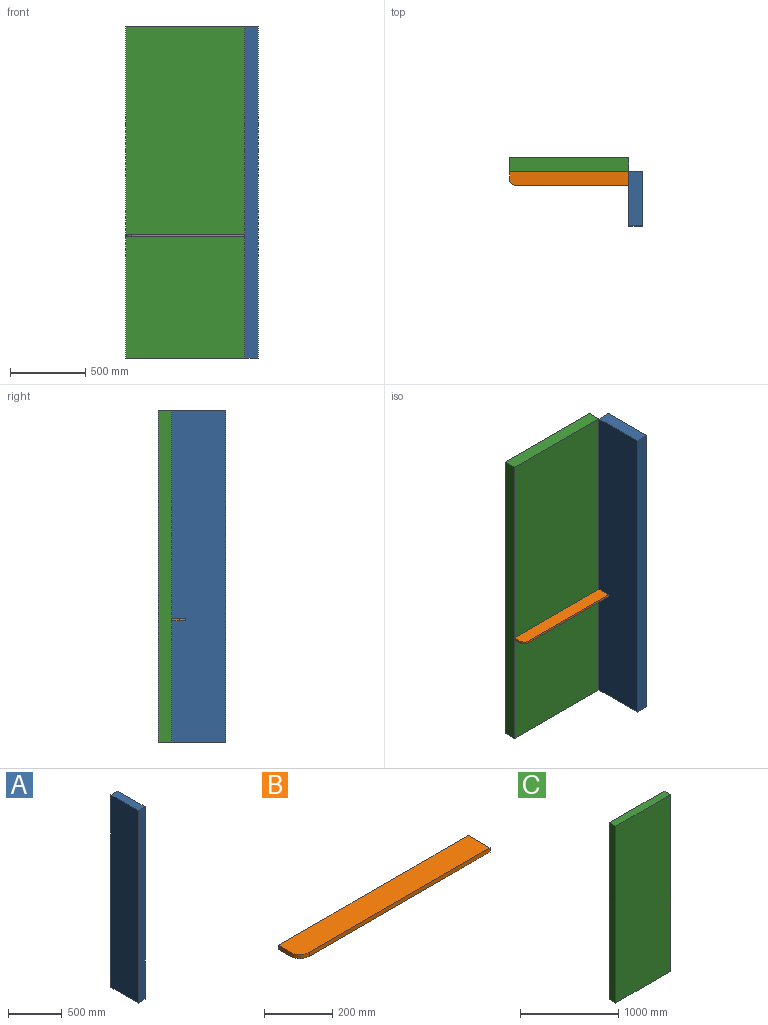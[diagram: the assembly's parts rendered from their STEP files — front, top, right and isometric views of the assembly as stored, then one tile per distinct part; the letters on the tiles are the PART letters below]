
ASSEMBLY  parts=3 mates=2
PART A: 6 faces, bbox 90x360x2200 mm
  f0: plane 360x90mm, normal (0,0,-1), area 32400mm2, adj f1,f3,f4,f5
  f1: plane 2200x90mm, normal (0,1,0), area 198000mm2, adj f0,f2,f4,f5
  f2: plane 360x90mm, normal (0,0,1), area 32400mm2, adj f1,f3,f4,f5
  f3: plane 2200x90mm, normal (0,-1,0), area 198000mm2, adj f0,f2,f4,f5
  f4: plane 2200x360mm, normal (1,0,0), area 792000mm2, adj f0,f1,f2,f3
  f5: plane 2200x360mm, normal (-1,0,0), area 792000mm2, adj f0,f1,f2,f3
PART B: 7 faces, bbox 790x90x15 mm
  f0: plane 50x15mm, normal (-1,0,0), area 750mm2, adj f1,f4,f5,f6
  f1: cylinder r=40mm len=40mm, axis (0,0,-1), area 942.5mm2, adj f0,f2,f5,f6
  f2: plane 750x15mm, normal (0,-1,0), area 11250mm2, adj f1,f3,f5,f6
  f3: plane 90x15mm, normal (1,0,0), area 1350mm2, adj f2,f4,f5,f6
  f4: plane 790x15mm, normal (0,1,0), area 11850mm2, adj f0,f3,f5,f6
  f5: plane 790x90mm, normal (0,0,1), area 70756.6mm2, adj f0,f1,f2,f3,f4
  f6: plane 790x90mm, normal (0,0,-1), area 70756.6mm2, adj f0,f1,f2,f3,f4
PART C: 6 faces, bbox 790x90x2200 mm
  f0: plane 2200x90mm, normal (-1,0,0), area 198000mm2, adj f1,f3,f4,f5
  f1: plane 790x90mm, normal (0,0,-1), area 71100mm2, adj f0,f2,f4,f5
  f2: plane 2200x90mm, normal (1,0,0), area 198000mm2, adj f1,f3,f4,f5
  f3: plane 790x90mm, normal (0,0,1), area 71100mm2, adj f0,f2,f4,f5
  f4: plane 2200x790mm, normal (0,1,0), area 1738000mm2, adj f0,f1,f2,f3
  f5: plane 2200x790mm, normal (0,-1,0), area 1738000mm2, adj f0,f1,f2,f3
PLACE A t=(-174.75,375.33,57.99)mm fixed
PLACE B t=(-569.33,329,174.65)mm
PLACE C t=(-174.75,375.33,57.99)mm fixed
MATE planar B.f4 <-> C.f5  axis (0,1,0) through (-174.33,375.33,182.15)mm
MATE planar A.f5 <-> B.f3  axis (-1,0,0) through (220.67,195.33,472.49)mm
